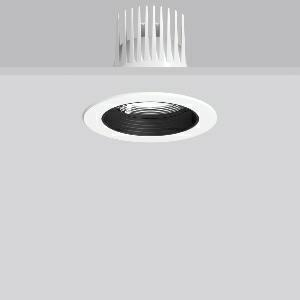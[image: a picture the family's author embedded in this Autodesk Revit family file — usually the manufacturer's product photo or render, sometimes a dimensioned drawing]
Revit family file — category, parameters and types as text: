
# Revit family: heledon_maxi_e_901761_002_3_76_70bf
name_source: partatom
category: Lighting Fixtures
units: mm (PartAtom-declared; Revit-internal decimal feet)

## family parameters
Cut with Voids When Loaded = No
Host = Face
Light Source = No
Part Type = Normal
Room Calculation Point = No
Round Connector Dimension = Use Diameter
Shared = No

## types (1)
- HELEDON maxi E (1 x LED Modul 935, 2800 lm, 3500)
    Apparent Load = 25 VA
    Approval mark = CE
    CIE Flux Codes = 96 100 100 100 100
    Color Rendering = 92
    Color Temperature = 3500
    Default Elevation = 1800 mm
    Description = Series: HELEDON maxi
Round recessed downlight. Housing: die-cast aluminium, powder-coated. Black plastic ring and recessed LED to prevent glare from the side. Optical assembly with lens made of plastic (polycarbonate) for the best homogeneous light distribution - can be changed without tools. Best colour rendering index Ra>90. Suitable for Recessed ceiling mounting. Installation without tools thanks to spring fastening system. Including separate LED converter with connecting cable 600 mm.High quality converter without flickering and stroboscopic effect. Through-wiring box (5 pole) available as accessory. The following accessories can be mounted without use of tools: interchangeable lenses, decorative glasses, honeycomb louvre, clear and frosted diffusers, white interchangeable plastic ring. 
Colour: traffic white, matt (RAL 9016)
Diameter: 162 mm
Height: 3 mm
Cut-out diameter: 152 mm
Recess height: 200 mm
Luminaire: recess height: 135 mm
Lamp: LED
Socket: without socket
Colour temperature: 3500K
Colour rendering index (CRI): 92
System power: 25 W
Rated luminous flux: 2800 lm
Luminous efficiency: 112 lm/W
Control gear: Converter, dimmable, DALI
Protection class: II
Type of protection: IP 20
    Height = 0 mm  [stored 0 ft]
    Lamp = 1 x LED Modul 935
    Lamp Light Flux = 2800 lm
    Lamp count = 1
    Length = 162 mm
    Lifetime = 50000 h
    Luminous efficacy = 112 lm/W
    Manufacturer = RZB
    ModVariant = No
    Model = 901761.002.3.76
    Mounting Place = Ceiling
    Mounting Type = Recessed
    Number of Poles = 1
    OnlyDefault = Yes
    Power Factor = 1
    Product Name = HELEDON maxi E
    Product group = Recessed downlights
    ProductGroupID = 402
    Protection Class = Protection class II
    Protection Degree = IP 20
    RLX_Detail_Level = 1
    RLX_Emergency_Light_Flux = 0 lm
    RLX_Emergency_Type = 0
    RLX_Emergency_Type_DB = No
    RlxData = <blob elided: 119581 chars, md5=0b04037e>
    Socket = socket
    Standby Power = 0 W
    System Light Flux = 2800 lm
    System Power = 25 W
    Type Comments = Product without accessories
    Type Image = 901663.002.jpg
    URL = http://relux.com
    VarID = ---
    Voltage = 230 V
    Voltage Range = 220-240 V
    Weight = 0.00 kg
    Width = 0 mm  [stored 0 ft]

note: [stored X ft] marks values corroborated as IEEE doubles in the binary element streams (Revit-internal decimal feet)

## geometry (parser evidence)
native form markers: Blend x4, Sweep x12
no freeform markers — native parametric forms only
